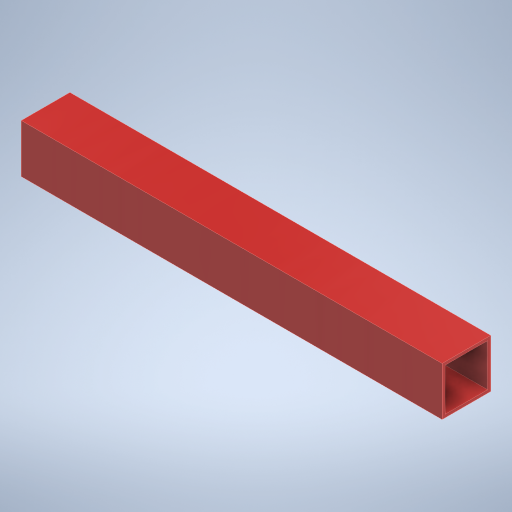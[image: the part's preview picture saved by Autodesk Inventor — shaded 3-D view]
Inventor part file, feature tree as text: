
AUTODESK INVENTOR PART (.ipt)
format: ipt  version: 2024 (Build 280153000, 153)  size: 229,376 bytes
history: native  units: in
note: dims shown in document units (in); Inventor stores cm internally (conversion verified against a paired STEP export)
features: extrude x1, sketch x1
ambient origin geometry x8: Origin, YZ Plane, XZ Plane, XY Plane, X Axis, Y Axis, Z Axis, Center Point
bodies: Solid1 (feature_tree)
feature tree (2):
  extrude  "Extrusion1"  Depth=1.0in
  sketch  "Sketch1"  dims[d0=1.0in d1=1.0in d2=0.0625in d3=8.6614in d4=0.0in]
